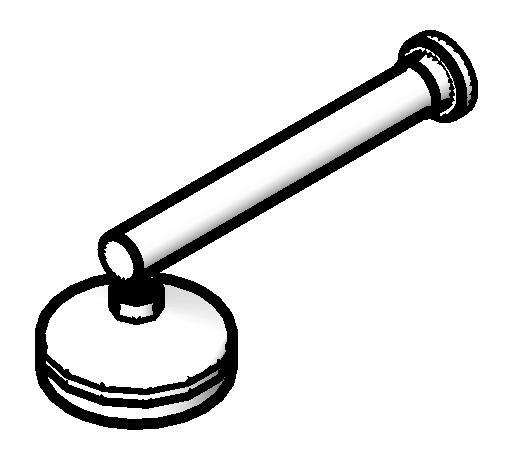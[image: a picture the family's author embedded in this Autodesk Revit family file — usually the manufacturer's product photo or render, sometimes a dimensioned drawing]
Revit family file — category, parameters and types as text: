
# Revit family: Deca_Chuveiro de Parede_AcquaPlus_1990.C.CT
name_source: partatom
category: Plumbing Fixtures
revit_build: Autodesk Revit Architecture 2012 (Build: 20110916_2132(x64)
units: mm (PartAtom-declared; Revit-internal decimal feet)

## types (1)
- 1990.C.CT
    Acompanha o Produto = Não Aplicável
    Aprovado por = Contino/quattroD
    Atendimento ao Cliente = 0800-011-7073
    Chuveiro = Deca CR10 Cromado Metal
    Consumo = Varia com a pressão (consultar catálogo)
    Criador por = Contino/quattroD
    Código = 1990.C.CT
    Default Elevation = 2100 mm
    Description = Chuveiro
    Descrição = Chuveiro
    Detalhes = Deca CZ87 Cinza Real Poliéster
    Diâmetro Ponto de Agua = 15 mm  [stored 0.0492126 ft]
    Fabricante = Deca
    Flow Pressure = 0.00 psi
    HWFU = 0
    Informações Complementares = Tubo parede / Pode ser usado com restritores de vazão de 8 (4266.061) 14 (4266.062) ou 16 (4266.059) litros por minuto
    Linha = AquaPlus
    Louça/Metais = Metais
    Manufacturer = Deca
    Material = Metal
    Model = 1990.C.CT
    Norma = NBR 15206
    Peso Liquido (Kg) = 1.392
    Pressão = 2 a 40 mca
    Produto = Chuveiro AquaPlus com tubo luxo
    Raio Ponto de Agua = 8 mm  [stored 0.0262467 ft]
    Segmento = Luxo
    URL = www.deca.com.br
    Vendido Separadamente = Não Aplicável

note: [stored X ft] marks values corroborated as IEEE doubles in the binary element streams (Revit-internal decimal feet)

## geometry (parser evidence)
native form markers: Blend x4, Sweep x2
no freeform markers — native parametric forms only
